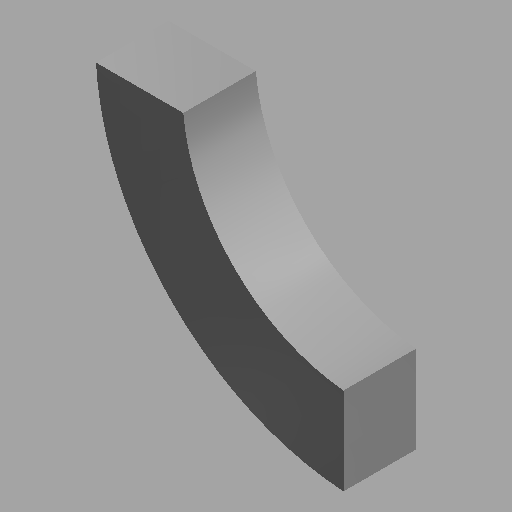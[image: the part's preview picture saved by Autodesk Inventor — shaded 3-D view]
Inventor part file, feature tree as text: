
AUTODESK INVENTOR PART (.ipt)
format: ipt  version: 2023 (Build 270158030, 158C)  size: 94,208 bytes
history: native  units: mm (DEFAULTED — no unit token found)
features: other x1, direct_edit x1, revolve x1
ambient origin geometry x8: Origin, YZ Plane, XZ Plane, XY Plane, X Axis, Y Axis, Z Axis, Center Point
bodies: Solid1 (feature_tree)
feature tree (3):
  other  "Arch header 3 (C)"
  direct_edit  "Direct Edit1"
  revolve  "Rotate1"  [1 undecoded]
note: 1 required parameter value undecoded (feature->parameter linkage not recoverable at this tier; creation-order binding heuristic only, values carry confidence <= 0.55)
